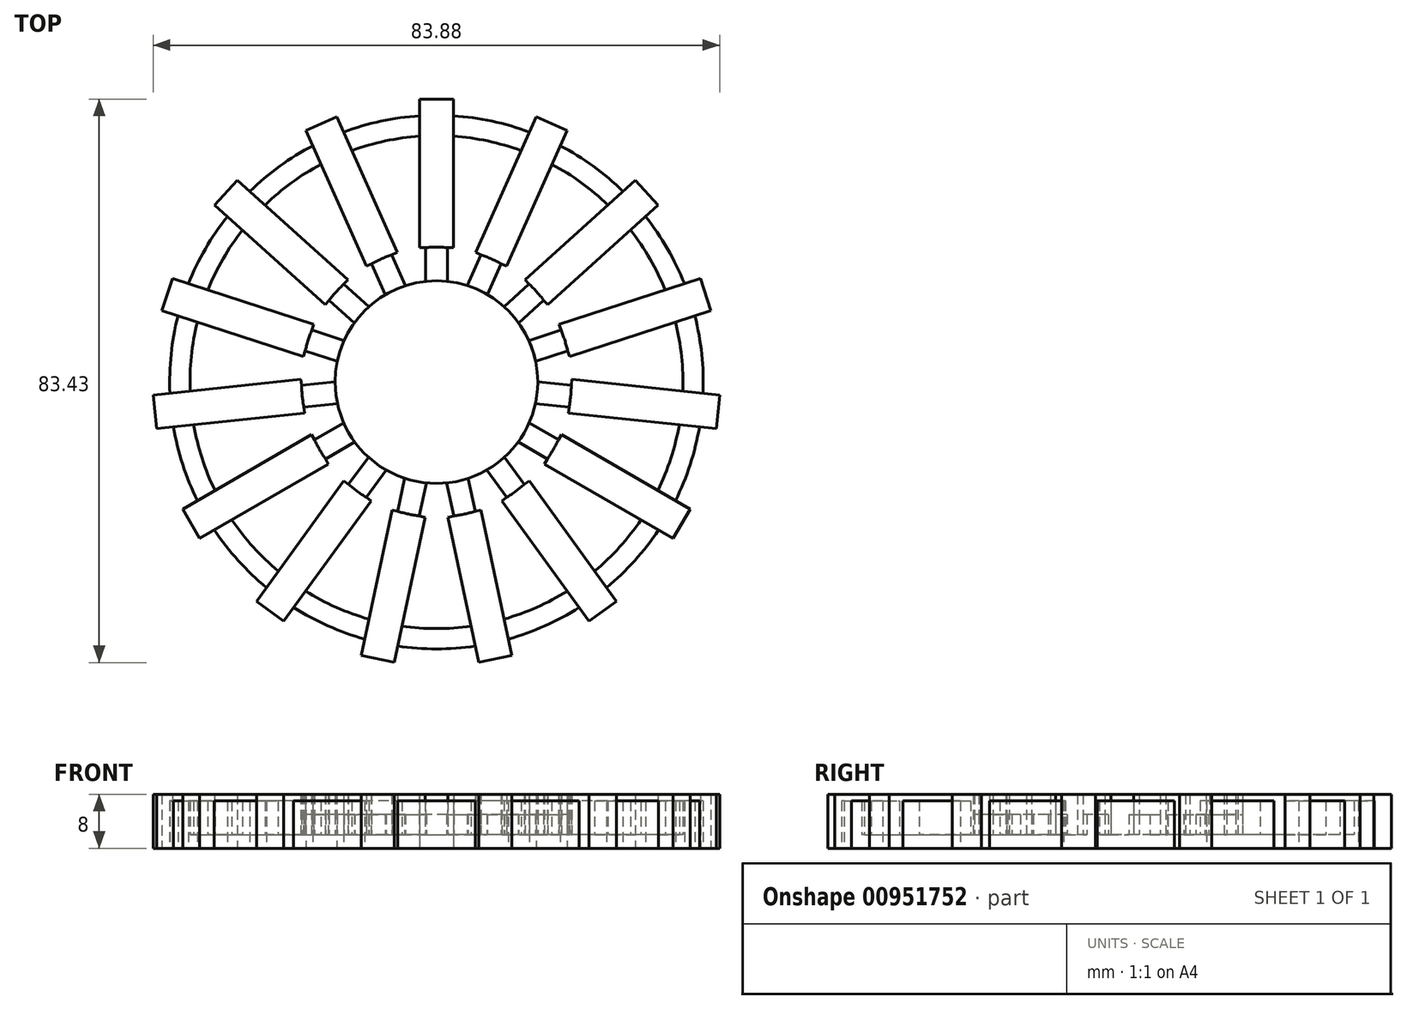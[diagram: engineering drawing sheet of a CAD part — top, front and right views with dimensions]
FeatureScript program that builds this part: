
annotation { "Feature Type Name" : "Feature", "Feature Type Description" : "" }
export const myFeature = defineFeature(function(context is Context, id is Id, definition is map)
    precondition{}
    {
        {
            var Q0;
            Q0=qCreatedBy(makeId("Top.planeOp"),FACE);
            var sketch = newSketch(context, id + "F0", { "sketchPlane" : qUnion([Q0])});
            skCircle(sketch, "E0", {"center": v(0, 0) * mm, "radius": 36.5 * mm});
            skCircle(sketch, "E1", {"center": v(0, 0) * mm, "radius": 39.5 * mm});
            skSolve(sketch);
        }
        {
            var Q0;
            Q0=makeQuery(id+"F0.imprint","IMPRINT",FACE,{"disambiguationData":[TD([[makeQuery(id+"F0.imprint","IMPRINT",EDGE,{"derivedFrom":sQuery(id+"F0.wireOp",EDGE,"E0")}),1.0]])]});
            extrude(context, id + "F1", {"entities" : qUnion([Q0]), "depth" : 2 * mm, "offsetDistance" : 25 * mm});
        }
        {
            var Q0;
            Q0 = qSketchRegion(id + "F0", true);
            extrude(context, id + "F2", {"entities" : qUnion([Q0]), "operationType" : NewBodyOperationType.ADD, "depth" : 7 * mm, "offsetDistance" : 25 * mm});
        }
        {
            var Q0;
            Q0=makeQuery(id+"F1.opExtrude","CAP_FACE",FACE,{"disambiguationData":[OSD([sQuery(id+"F0.wireOp",EDGE,"E0")])],"isStart":false});
            var sketch = newSketch(context, id + "F3", { "sketchPlane" : qUnion([Q0])});
            skCircle(sketch, "E2", {"center": v(0, 0) * mm, "radius": 15 * mm});
            skLineSegment(sketch, "E3.bottom", {"start": v(-1.62, 14.91) * mm, "end": v(1.63, 14.91) * mm});
            skLineSegment(sketch, "E3.top", {"start": v(-1.62, 19.91) * mm, "end": v(1.63, 19.91) * mm});
            skLineSegment(sketch, "E3.left", {"start": v(-1.62, 14.91) * mm, "end": v(-1.62, 19.91) * mm});
            skLineSegment(sketch, "E3.right", {"start": v(1.63, 14.91) * mm, "end": v(1.63, 19.91) * mm});
            skPoint(sketch, "E3.middle", {"position": v(0, 17.41) * mm});
            skLineSegment(sketch, "E4.bottom", {"start": v(-2.5, 19.91) * mm, "end": v(2.5, 19.91) * mm});
            skLineSegment(sketch, "E4.top", {"start": v(-2.5, 41.91) * mm, "end": v(2.5, 41.91) * mm});
            skLineSegment(sketch, "E4.left", {"start": v(-2.5, 19.91) * mm, "end": v(-2.5, 41.91) * mm});
            skLineSegment(sketch, "E4.right", {"start": v(2.5, 19.91) * mm, "end": v(2.5, 41.91) * mm});
            skPoint(sketch, "E4.middle", {"position": v(0, 30.91) * mm});
            skCircle(sketch, "E5", {"center": v(0, 0) * mm, "radius": 30.79 * mm, "construction": true});
            skSolve(sketch);
        }
        {
            var Q0;
            {var subQ0=sQuery(id+"F3.wireOp",EDGE,"E3.bottom");Q0=makeQuery(id+"F3.imprint","IMPRINT",FACE,{"disambiguationData":[TD([[makeQuery(id+"F3.imprint","IMPRINT",EDGE,{"derivedFrom":subQ0}),1.0]])]});}
            var Q1;
            {var subQ0=sQuery(id+"F3.wireOp",EDGE,"E3.left");Q1=makeQuery(id+"F3.imprint","IMPRINT",FACE,{"disambiguationData":[TD([[makeQuery(id+"F3.imprint","IMPRINT",EDGE,{"derivedFrom":subQ0}),-1.0]])]});}
            var Q2;
            {var subQ0=sQuery(id+"F3.wireOp",EDGE,"E4.top");Q2=makeQuery(id+"F3.imprint","IMPRINT",FACE,{"disambiguationData":[TD([[makeQuery(id+"F3.imprint","IMPRINT",EDGE,{"derivedFrom":subQ0}),-1.0]])]});}
            var Q3;
            {var subQ0=sQuery(id+"F3.wireOp",EDGE,"E3.bottom");Q3=makeQuery(id+"F3.imprint","IMPRINT",FACE,{"disambiguationData":[TD([[makeQuery(id+"F3.imprint","IMPRINT",EDGE,{"derivedFrom":subQ0}),-1.0]])]});}
            var Q4;
            {var subQ1=sQuery(id+"F3.wireOp",EDGE,"E4.bottom");var subQ8=makeQuery(id+"F3.imprint","INTERSECT",VERTEX,{"derivedFrom":[sQuery(id+"F3.wireOp",EDGE,"E3.left"),subQ1]});Q4=makeQuery(id+"F3.imprint","IMPRINT",FACE,{"disambiguationData":[TD([[makeQuery(id+"F3.imprint","IMPRINT",EDGE,{"disambiguationData":[TD([[subQ8,1.0]])],"derivedFrom":subQ1}),1.0]])]});}
            extrude(context, id + "F4", {"entities" : qUnion([Q0, Q1, Q2, Q3, Q4]), "operationType" : NewBodyOperationType.ADD, "depth" : 6 * mm, "offsetDistance" : 25 * mm, "hasSecondDirection" : true, "secondDirectionOppositeDirection" : true, "secondDirectionDepth" : 2 * mm});
        }
        {
            var Q0;
            Q0=makeQuery(id+"F1.opExtrude","SWEPT_BODY",BODY,{"disambiguationData":[OSD([sQuery(id+"F0.wireOp",EDGE,"E0")])]});
            var Q1;
            Q1=sQuery(id+"F0.wireOp",EDGE,"E0");
            circularPattern(context, id + "F5", {"entities" : qUnion([Q0]), "axis" : qUnion([Q1]), "angle" : 360 * degree, "instanceCount" : 15, "equalSpace" : true});
        }
        {
            var Q0;
            Q0=makeQuery(id+"F5.opPattern","COPY",BODY,{"derivedFrom":makeQuery(id+"F1.opExtrude","SWEPT_BODY",BODY,{"disambiguationData":[OSD([sQuery(id+"F0.wireOp",EDGE,"E0")])]}),"instanceName":"8"});
            var Q1;
            Q1=makeQuery(id+"F5.opPattern","COPY",BODY,{"derivedFrom":makeQuery(id+"F1.opExtrude","SWEPT_BODY",BODY,{"disambiguationData":[OSD([sQuery(id+"F0.wireOp",EDGE,"E0")])]}),"instanceName":"10"});
            var Q2;
            Q2=makeQuery(id+"F5.opPattern","COPY",BODY,{"derivedFrom":makeQuery(id+"F1.opExtrude","SWEPT_BODY",BODY,{"disambiguationData":[OSD([sQuery(id+"F0.wireOp",EDGE,"E0")])]}),"instanceName":"11"});
            var Q3;
            Q3=makeQuery(id+"F5.opPattern","COPY",BODY,{"derivedFrom":makeQuery(id+"F1.opExtrude","SWEPT_BODY",BODY,{"disambiguationData":[OSD([sQuery(id+"F0.wireOp",EDGE,"E0")])]}),"instanceName":"12"});
            var Q4;
            Q4=makeQuery(id+"F5.opPattern","COPY",BODY,{"derivedFrom":makeQuery(id+"F1.opExtrude","SWEPT_BODY",BODY,{"disambiguationData":[OSD([sQuery(id+"F0.wireOp",EDGE,"E0")])]}),"instanceName":"13"});
            var Q5;
            Q5=makeQuery(id+"F5.opPattern","COPY",BODY,{"derivedFrom":makeQuery(id+"F1.opExtrude","SWEPT_BODY",BODY,{"disambiguationData":[OSD([sQuery(id+"F0.wireOp",EDGE,"E0")])]}),"instanceName":"3"});
            var Q6;
            Q6=makeQuery(id+"F5.opPattern","COPY",BODY,{"derivedFrom":makeQuery(id+"F1.opExtrude","SWEPT_BODY",BODY,{"disambiguationData":[OSD([sQuery(id+"F0.wireOp",EDGE,"E0")])]}),"instanceName":"4"});
            var Q7;
            Q7=makeQuery(id+"F5.opPattern","COPY",BODY,{"derivedFrom":makeQuery(id+"F1.opExtrude","SWEPT_BODY",BODY,{"disambiguationData":[OSD([sQuery(id+"F0.wireOp",EDGE,"E0")])]}),"instanceName":"5"});
            var Q8;
            Q8=makeQuery(id+"F5.opPattern","COPY",BODY,{"derivedFrom":makeQuery(id+"F1.opExtrude","SWEPT_BODY",BODY,{"disambiguationData":[OSD([sQuery(id+"F0.wireOp",EDGE,"E0")])]}),"instanceName":"6"});
            booleanBodies(context, id + "F6", {"operationType" : BooleanOperationType.UNION, "tools" : qUnion([Q0, Q1, Q2, Q3, Q4, Q5, Q6, Q7, Q8])});
        }
        {
            var Q0;
            Q0=makeQuery(id+"F1.opExtrude","SWEPT_BODY",BODY,{"disambiguationData":[OSD([sQuery(id+"F0.wireOp",EDGE,"E0")])]});
            var Q1;
            Q1=makeQuery(id+"F5.opPattern","COPY",BODY,{"derivedFrom":makeQuery(id+"F1.opExtrude","SWEPT_BODY",BODY,{"disambiguationData":[OSD([sQuery(id+"F0.wireOp",EDGE,"E0")])]}),"instanceName":"1"});
            var Q2;
            Q2=makeQuery(id+"F5.opPattern","COPY",BODY,{"derivedFrom":makeQuery(id+"F1.opExtrude","SWEPT_BODY",BODY,{"disambiguationData":[OSD([sQuery(id+"F0.wireOp",EDGE,"E0")])]}),"instanceName":"7"});
            var Q3;
            Q3=makeQuery(id+"F5.opPattern","COPY",BODY,{"derivedFrom":makeQuery(id+"F1.opExtrude","SWEPT_BODY",BODY,{"disambiguationData":[OSD([sQuery(id+"F0.wireOp",EDGE,"E0")])]}),"instanceName":"8"});
            booleanBodies(context, id + "F7", {"operationType" : BooleanOperationType.UNION, "tools" : qUnion([Q0, Q1, Q2, Q3])});
        }
        {
            var Q0;
            Q0=makeQuery(id+"F1.opExtrude","SWEPT_BODY",BODY,{"disambiguationData":[OSD([sQuery(id+"F0.wireOp",EDGE,"E0")])]});
            var Q1;
            Q1=makeQuery(id+"F5.opPattern","COPY",BODY,{"derivedFrom":makeQuery(id+"F1.opExtrude","SWEPT_BODY",BODY,{"disambiguationData":[OSD([sQuery(id+"F0.wireOp",EDGE,"E0")])]}),"instanceName":"2"});
            var Q2;
            Q2=makeQuery(id+"F5.opPattern","COPY",BODY,{"derivedFrom":makeQuery(id+"F1.opExtrude","SWEPT_BODY",BODY,{"disambiguationData":[OSD([sQuery(id+"F0.wireOp",EDGE,"E0")])]}),"instanceName":"9"});
            booleanBodies(context, id + "F8", {"operationType" : BooleanOperationType.UNION, "tools" : qUnion([Q0, Q1, Q2])});
        }
        {
            var Q0;
            Q0=makeQuery(id+"F5.opPattern","COPY",FACE,{"derivedFrom":makeQuery(id+"F4.opExtrude","CAP_FACE",FACE,{"disambiguationData":[OSD([sQuery(id+"F3.wireOp",EDGE,"E2"),sQuery(id+"F3.wireOp",EDGE,"E3.left"),sQuery(id+"F3.wireOp",EDGE,"E3.right"),sQuery(id+"F3.wireOp",EDGE,"E4.bottom"),sQuery(id+"F3.wireOp",EDGE,"E4.top"),sQuery(id+"F3.wireOp",EDGE,"E4.left"),sQuery(id+"F3.wireOp",EDGE,"E4.right")])],"isStart":false}),"instanceName":"14"});
            var sketch = newSketch(context, id + "F9", { "sketchPlane" : qUnion([Q0])});
            skCircle(sketch, "E6", {"center": v(0, 0) * mm, "radius": 15 * mm});
            skCircle(sketch, "E7", {"center": v(0, 0) * mm, "radius": 19.98 * mm});
            skSolve(sketch);
        }
        {
            var Q0;
            Q0 = qSketchRegion(id + "F9", true);
            extrude(context, id + "F10", {"entities" : qUnion([Q0]), "operationType" : NewBodyOperationType.REMOVE, "oppositeDirection" : true, "depth" : 3 * mm, "offsetDistance" : 25 * mm});
        }
        {
            var Q0;
            Q0=makeQuery(id+"F1.opExtrude","SWEPT_BODY",BODY,{"disambiguationData":[OSD([sQuery(id+"F0.wireOp",EDGE,"E0")])]});
            var Q1;
            Q1=makeQuery(id+"F5.opPattern","COPY",BODY,{"derivedFrom":makeQuery(id+"F1.opExtrude","SWEPT_BODY",BODY,{"disambiguationData":[OSD([sQuery(id+"F0.wireOp",EDGE,"E0")])]}),"instanceName":"14"});
            booleanBodies(context, id + "F11", {"operationType" : BooleanOperationType.UNION, "tools" : qUnion([Q0, Q1])});
        }
        {
            var Q0;
            Q0=qCreatedBy(makeId("Top.planeOp"),FACE);
            var Q1;
            {var subQ0=sQuery(id+"F3.wireOp",EDGE,"E2");var subQ1=makeQuery(id+"F4.opExtrude","CAP_FACE",FACE,{"disambiguationData":[OSD([subQ0,sQuery(id+"F3.wireOp",EDGE,"E3.left"),sQuery(id+"F3.wireOp",EDGE,"E3.right"),sQuery(id+"F3.wireOp",EDGE,"E4.bottom"),sQuery(id+"F3.wireOp",EDGE,"E4.top"),sQuery(id+"F3.wireOp",EDGE,"E4.left"),sQuery(id+"F3.wireOp",EDGE,"E4.right")])],"isStart":false});Q1=makeQuery(id+"F11.opBoolean","MERGE",FACE,{"derivedFrom":[makeQuery(id+"F5.opPattern","COPY",FACE,{"derivedFrom":subQ1,"instanceName":"14"}),makeQuery(id+"F10.boolean.opBoolean","SPLIT",FACE,{"disambiguationData":[TD([makeQuery(id+"F4.opExtrude","SWEPT_FACE",FACE,{"disambiguationData":[OSD([subQ0])]})])],"derivedFrom":makeQuery(id+"F8.opBoolean","MERGE",FACE,{"derivedFrom":[makeQuery(id+"F5.opPattern","COPY",FACE,{"derivedFrom":subQ1,"instanceName":"2"}),makeQuery(id+"F5.opPattern","COPY",FACE,{"derivedFrom":subQ1,"instanceName":"9"}),makeQuery(id+"F7.opBoolean","MERGE",FACE,{"derivedFrom":[subQ1,makeQuery(id+"F5.opPattern","COPY",FACE,{"derivedFrom":subQ1,"instanceName":"1"}),makeQuery(id+"F5.opPattern","COPY",FACE,{"derivedFrom":subQ1,"instanceName":"7"}),makeQuery(id+"F6.opBoolean","MERGE",FACE,{"derivedFrom":[makeQuery(id+"F5.opPattern","COPY",FACE,{"derivedFrom":subQ1,"instanceName":"3"}),makeQuery(id+"F5.opPattern","COPY",FACE,{"derivedFrom":subQ1,"instanceName":"4"}),makeQuery(id+"F5.opPattern","COPY",FACE,{"derivedFrom":subQ1,"instanceName":"5"}),makeQuery(id+"F5.opPattern","COPY",FACE,{"derivedFrom":subQ1,"instanceName":"6"}),makeQuery(id+"F5.opPattern","COPY",FACE,{"derivedFrom":subQ1,"instanceName":"8"}),makeQuery(id+"F5.opPattern","COPY",FACE,{"derivedFrom":subQ1,"instanceName":"10"}),makeQuery(id+"F5.opPattern","COPY",FACE,{"derivedFrom":subQ1,"instanceName":"11"}),makeQuery(id+"F5.opPattern","COPY",FACE,{"derivedFrom":subQ1,"instanceName":"12"}),makeQuery(id+"F5.opPattern","COPY",FACE,{"derivedFrom":subQ1,"instanceName":"13"})]})]})]})})]});}
            var sketch = newSketch(context, id + "F12", { "sketchPlane" : qUnion([Q0, Q1])});
            skCircle(sketch, "E8", {"center": v(0, 0) * mm, "radius": 19.84 * mm});
            skCircle(sketch, "E9", {"center": v(0, 0) * mm, "radius": 15 * mm});
            skSolve(sketch);
        }
        {
            var Q0;
            Q0 = qSketchRegion(id + "F12", true);
            extrude(context, id + "F13", {"entities" : qUnion([Q0]), "operationType" : NewBodyOperationType.REMOVE, "oppositeDirection" : true, "depth" : 3 * mm, "offsetDistance" : 25 * mm});
        }
    });
